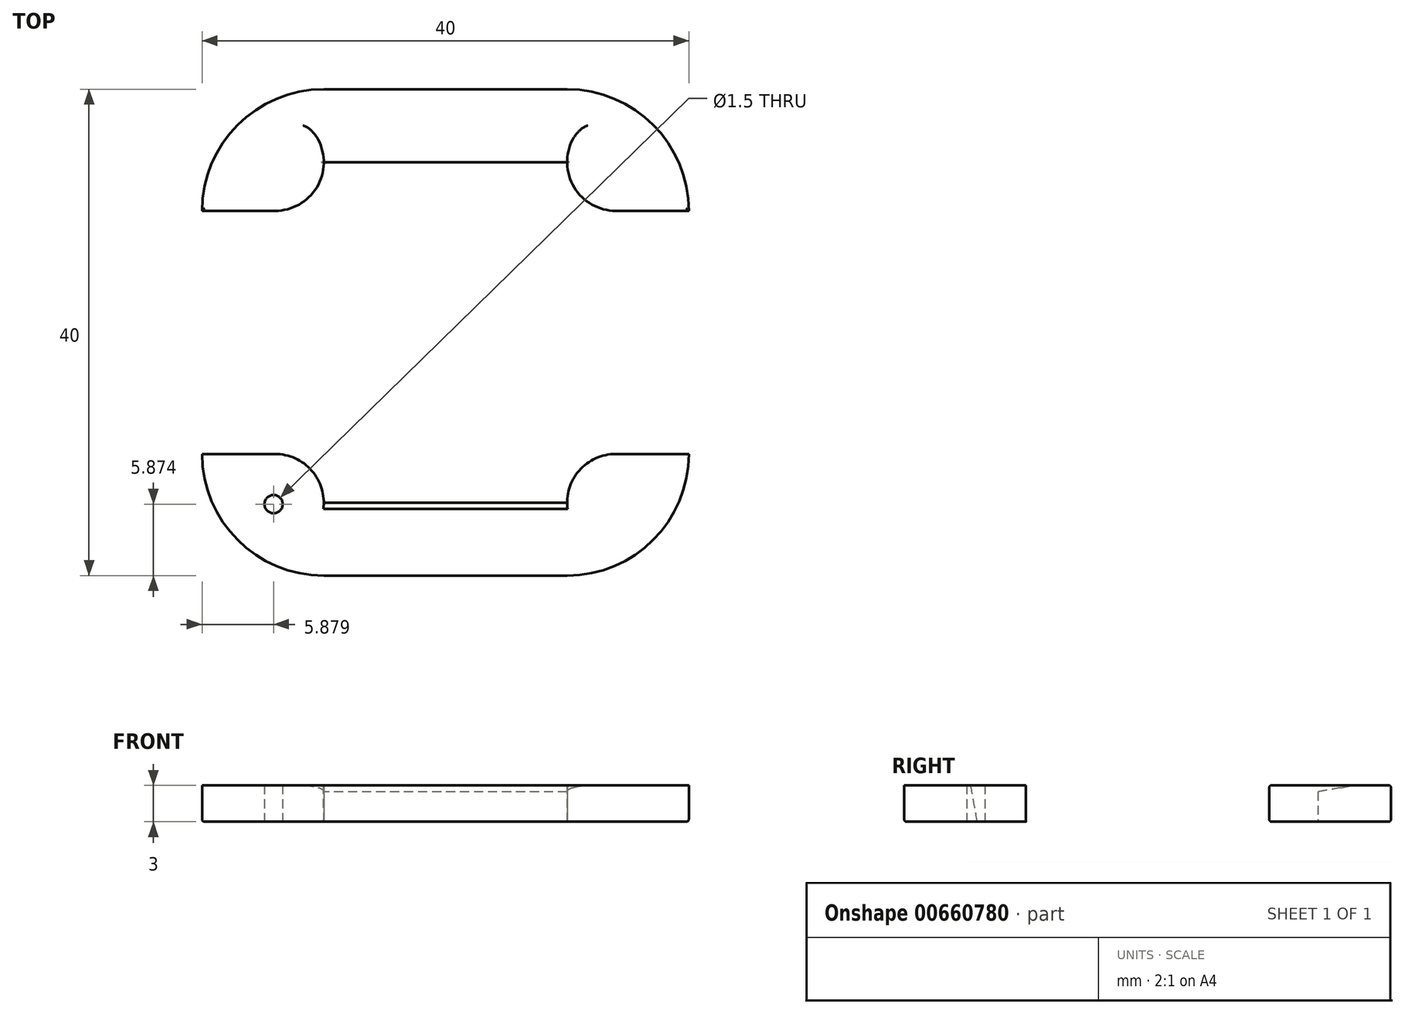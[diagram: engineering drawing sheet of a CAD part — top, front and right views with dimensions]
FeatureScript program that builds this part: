
annotation { "Feature Type Name" : "Feature", "Feature Type Description" : "" }
export const myFeature = defineFeature(function(context is Context, id is Id, definition is map)
    precondition{}
    {
        {
            var Q0;
            Q0=qCreatedBy(makeId("Top.planeOp"),FACE);
            var sketch = newSketch(context, id + "F0", { "sketchPlane" : qUnion([Q0])});
            skLineSegment(sketch, "E0.bottom", {"start": v(-41.1, 15.45) * mm, "end": v(-31.1, 15.45) * mm});
            skLineSegment(sketch, "E0.top", {"start": v(-41.1, 5.45) * mm, "end": v(-31.1, 5.45) * mm});
            skLineSegment(sketch, "E0.left", {"start": v(-41.1, 15.45) * mm, "end": v(-41.1, 5.45) * mm});
            skLineSegment(sketch, "E0.right", {"start": v(-31.1, 15.45) * mm, "end": v(-31.1, 5.45) * mm});
            skLineSegment(sketch, "E1.bottom", {"start": v(-31.1, 15.45) * mm, "end": v(-11.1, 15.45) * mm});
            skLineSegment(sketch, "E1.top", {"start": v(-31.1, 9.45) * mm, "end": v(-11.1, 9.45) * mm});
            skLineSegment(sketch, "E1.left", {"start": v(-31.1, 15.45) * mm, "end": v(-31.1, 9.45) * mm});
            skLineSegment(sketch, "E1.right", {"start": v(-11.1, 15.45) * mm, "end": v(-11.1, 9.45) * mm});
            skLineSegment(sketch, "E2.bottom", {"start": v(-11.1, 15.45) * mm, "end": v(-1.1, 15.45) * mm});
            skLineSegment(sketch, "E2.top", {"start": v(-11.1, 5.45) * mm, "end": v(-1.1, 5.45) * mm});
            skLineSegment(sketch, "E2.left", {"start": v(-11.1, 15.45) * mm, "end": v(-11.1, 5.45) * mm});
            skLineSegment(sketch, "E2.right", {"start": v(-1.1, 15.45) * mm, "end": v(-1.1, 5.45) * mm});
            skLineSegment(sketch, "E3.bottom", {"start": v(-7.1, 5.45) * mm, "end": v(-1.1, 5.45) * mm});
            skLineSegment(sketch, "E3.top", {"start": v(-7.1, -14.55) * mm, "end": v(-1.1, -14.55) * mm});
            skLineSegment(sketch, "E3.left", {"start": v(-7.1, 5.45) * mm, "end": v(-7.1, -14.55) * mm});
            skLineSegment(sketch, "E3.right", {"start": v(-1.1, 5.45) * mm, "end": v(-1.1, -14.55) * mm});
            skLineSegment(sketch, "E4.bottom", {"start": v(-11.1, -14.55) * mm, "end": v(-1.1, -14.55) * mm});
            skLineSegment(sketch, "E4.top", {"start": v(-11.1, -24.55) * mm, "end": v(-1.1, -24.55) * mm});
            skLineSegment(sketch, "E4.left", {"start": v(-11.1, -14.55) * mm, "end": v(-11.1, -24.55) * mm});
            skLineSegment(sketch, "E4.right", {"start": v(-1.1, -14.55) * mm, "end": v(-1.1, -24.55) * mm});
            skLineSegment(sketch, "E5.bottom", {"start": v(-31.1, -18.55) * mm, "end": v(-11.1, -18.55) * mm});
            skLineSegment(sketch, "E5.top", {"start": v(-31.1, -24.55) * mm, "end": v(-11.1, -24.55) * mm});
            skLineSegment(sketch, "E5.left", {"start": v(-31.1, -18.55) * mm, "end": v(-31.1, -24.55) * mm});
            skLineSegment(sketch, "E5.right", {"start": v(-11.1, -18.55) * mm, "end": v(-11.1, -24.55) * mm});
            skLineSegment(sketch, "E6.bottom", {"start": v(-41.1, -14.55) * mm, "end": v(-31.1, -14.55) * mm});
            skLineSegment(sketch, "E6.top", {"start": v(-41.1, -24.55) * mm, "end": v(-31.1, -24.55) * mm});
            skLineSegment(sketch, "E6.left", {"start": v(-41.1, -14.55) * mm, "end": v(-41.1, -24.55) * mm});
            skLineSegment(sketch, "E6.right", {"start": v(-31.1, -14.55) * mm, "end": v(-31.1, -24.55) * mm});
            skLineSegment(sketch, "E7.bottom", {"start": v(-41.1, 5.45) * mm, "end": v(-35.1, 5.45) * mm});
            skLineSegment(sketch, "E7.top", {"start": v(-41.1, -14.55) * mm, "end": v(-35.1, -14.55) * mm});
            skLineSegment(sketch, "E7.left", {"start": v(-41.1, 5.45) * mm, "end": v(-41.1, -14.55) * mm});
            skLineSegment(sketch, "E7.right", {"start": v(-35.1, 5.45) * mm, "end": v(-35.1, -14.55) * mm});
            skCircle(sketch, "E8", {"center": v(-35.22, -18.68) * mm, "radius": 0.75 * mm});
            skSolve(sketch);
        }
        {
            var Q0;
            Q0=makeQuery(id+"F0.imprint","IMPRINT",FACE,{"disambiguationData":[TD([[makeQuery(id+"F0.imprint","IMPRINT",EDGE,{"derivedFrom":sQuery(id+"F0.wireOp",EDGE,"E0.bottom")}),-1.0]])]});
            var Q1;
            {var subQ0=sQuery(id+"F0.wireOp",EDGE,"E1.bottom");Q1=makeQuery(id+"F0.imprint","IMPRINT",FACE,{"disambiguationData":[TD([[makeQuery(id+"F0.imprint","IMPRINT",EDGE,{"derivedFrom":subQ0}),-1.0]])]});}
            var Q2;
            {var subQ3=sQuery(id+"F0.wireOp",EDGE,"E2.bottom");Q2=makeQuery(id+"F0.imprint","IMPRINT",FACE,{"disambiguationData":[TD([[makeQuery(id+"F0.imprint","IMPRINT",EDGE,{"derivedFrom":subQ3}),-1.0]])]});}
            var Q3;
            Q3=makeQuery(id+"F0.imprint","IMPRINT",FACE,{"disambiguationData":[TD([[makeQuery(id+"F0.imprint","IMPRINT",EDGE,{"derivedFrom":sQuery(id+"F0.wireOp",EDGE,"E3.bottom")}),-1.0]])]});
            var Q4;
            Q4=makeQuery(id+"F0.imprint","IMPRINT",FACE,{"disambiguationData":[TD([[makeQuery(id+"F0.imprint","IMPRINT",EDGE,{"derivedFrom":sQuery(id+"F0.wireOp",EDGE,"E4.top")}),1.0]])]});
            var Q5;
            {var subQ0=sQuery(id+"F0.wireOp",EDGE,"E5.bottom");Q5=makeQuery(id+"F0.imprint","IMPRINT",FACE,{"disambiguationData":[TD([[makeQuery(id+"F0.imprint","IMPRINT",EDGE,{"derivedFrom":subQ0}),-1.0]])]});}
            var Q6;
            {var subQ2=sQuery(id+"F0.wireOp",EDGE,"E6.bottom");Q6=makeQuery(id+"F0.imprint","IMPRINT",FACE,{"disambiguationData":[TD([[makeQuery(id+"F0.imprint","IMPRINT",EDGE,{"derivedFrom":subQ2}),-1.0]])]});}
            var Q7;
            Q7=makeQuery(id+"F0.imprint","IMPRINT",FACE,{"disambiguationData":[TD([[makeQuery(id+"F0.imprint","IMPRINT",EDGE,{"derivedFrom":sQuery(id+"F0.wireOp",EDGE,"E7.bottom")}),-1.0]])]});
            extrude(context, id + "F1", {"entities" : qUnion([Q0, Q1, Q2, Q3, Q4, Q5, Q6, Q7]), "depth" : 3 * mm, "offsetDistance" : 25 * mm});
        }
        {
            var Q0;
            Q0=makeQuery(id+"F1.opExtrude","SWEPT_EDGE",EDGE,{"disambiguationData":[OSD([sQuery(id+"F0.wireOp",EDGE,"E6.top"),sQuery(id+"F0.wireOp",EDGE,"E6.left")])]});
            var Q1;
            Q1=makeQuery(id+"F1.opExtrude","SWEPT_EDGE",EDGE,{"disambiguationData":[OSD([sQuery(id+"F0.wireOp",EDGE,"E4.top"),sQuery(id+"F0.wireOp",EDGE,"E4.right")])]});
            var Q2;
            Q2=makeQuery(id+"F1.opExtrude","SWEPT_EDGE",EDGE,{"disambiguationData":[OSD([sQuery(id+"F0.wireOp",EDGE,"E2.bottom"),sQuery(id+"F0.wireOp",EDGE,"E2.right")])]});
            var Q3;
            Q3=makeQuery(id+"F1.opExtrude","SWEPT_EDGE",EDGE,{"disambiguationData":[OSD([sQuery(id+"F0.wireOp",EDGE,"E0.bottom"),sQuery(id+"F0.wireOp",EDGE,"E0.left")])]});
            fillet(context, id + "F2", {"entities" : qUnion([Q0, Q1, Q2, Q3]), "radius" : 10 * mm, "tangentPropagation" : true, "allowEdgeOverflow" : false});
        }
        {
            var Q0;
            Q0=makeQuery(id+"F1.opExtrude","SWEPT_EDGE",EDGE,{"disambiguationData":[OSD([sQuery(id+"F0.wireOp",EDGE,"E0.top"),sQuery(id+"F0.wireOp",EDGE,"E0.right")])]});
            var Q1;
            Q1=makeQuery(id+"F1.opExtrude","SWEPT_EDGE",EDGE,{"disambiguationData":[OSD([sQuery(id+"F0.wireOp",EDGE,"E2.top"),sQuery(id+"F0.wireOp",EDGE,"E2.left")])]});
            var Q2;
            Q2=makeQuery(id+"F1.opExtrude","SWEPT_EDGE",EDGE,{"disambiguationData":[OSD([sQuery(id+"F0.wireOp",EDGE,"E4.bottom"),sQuery(id+"F0.wireOp",EDGE,"E4.left")])]});
            var Q3;
            Q3=makeQuery(id+"F1.opExtrude","SWEPT_EDGE",EDGE,{"disambiguationData":[OSD([sQuery(id+"F0.wireOp",EDGE,"E6.bottom"),sQuery(id+"F0.wireOp",EDGE,"E6.right")])]});
            fillet(context, id + "F3", {"entities" : qUnion([Q0, Q1, Q2, Q3]), "radius" : 4 * mm, "tangentPropagation" : true, "allowEdgeOverflow" : false});
        }
        {
            var Q0;
            Q0=makeQuery(id+"F1.opExtrude","CAP_EDGE",EDGE,{"disambiguationData":[OSD([sQuery(id+"F0.wireOp",EDGE,"E7.right")])],"isStart":false});
            var Q1;
            Q1=makeQuery(id+"F1.opExtrude","CAP_EDGE",EDGE,{"disambiguationData":[OSD([sQuery(id+"F0.wireOp",EDGE,"E1.top")])],"isStart":false});
            var Q2;
            Q2=makeQuery(id+"F1.opExtrude","CAP_EDGE",EDGE,{"disambiguationData":[OSD([sQuery(id+"F0.wireOp",EDGE,"E3.left")])],"isStart":false});
            var Q3;
            Q3=makeQuery(id+"F1.opExtrude","CAP_EDGE",EDGE,{"disambiguationData":[OSD([sQuery(id+"F0.wireOp",EDGE,"E5.bottom")])],"isStart":false});
            chamfer(context, id + "F4", {"entities" : qUnion([Q0, Q1, Q2, Q3]), "chamferType" : ChamferType.OFFSET_ANGLE, "width" : 3 * mm, "oppositeDirection" : false, "angle" : 10 * degree, "tangentPropagation" : true});
        }
        {
            var Q0;
            Q0=makeQuery(id+"F1.opExtrude","CAP_EDGE",EDGE,{"disambiguationData":[OSD([sQuery(id+"F0.wireOp",EDGE,"E4.top"),sQuery(id+"F0.wireOp",EDGE,"E5.top"),sQuery(id+"F0.wireOp",EDGE,"E6.top")])],"isStart":true});
            var Q1;
            Q1=makeQuery(id+"F1.opExtrude","CAP_FACE",FACE,{"disambiguationData":[OSD([sQuery(id+"F0.wireOp",EDGE,"E0.bottom"),sQuery(id+"F0.wireOp",EDGE,"E0.top"),sQuery(id+"F0.wireOp",EDGE,"E0.left"),sQuery(id+"F0.wireOp",EDGE,"E0.right"),sQuery(id+"F0.wireOp",EDGE,"E1.bottom"),sQuery(id+"F0.wireOp",EDGE,"E1.top"),sQuery(id+"F0.wireOp",EDGE,"E2.bottom"),sQuery(id+"F0.wireOp",EDGE,"E2.top"),sQuery(id+"F0.wireOp",EDGE,"E2.left"),sQuery(id+"F0.wireOp",EDGE,"E2.right"),sQuery(id+"F0.wireOp",EDGE,"E3.left"),sQuery(id+"F0.wireOp",EDGE,"E3.right"),sQuery(id+"F0.wireOp",EDGE,"E4.bottom"),sQuery(id+"F0.wireOp",EDGE,"E4.top"),sQuery(id+"F0.wireOp",EDGE,"E4.left"),sQuery(id+"F0.wireOp",EDGE,"E4.right"),sQuery(id+"F0.wireOp",EDGE,"E5.bottom"),sQuery(id+"F0.wireOp",EDGE,"E5.top"),sQuery(id+"F0.wireOp",EDGE,"E6.bottom"),sQuery(id+"F0.wireOp",EDGE,"E6.top"),sQuery(id+"F0.wireOp",EDGE,"E6.left"),sQuery(id+"F0.wireOp",EDGE,"E6.right"),sQuery(id+"F0.wireOp",EDGE,"E7.left"),sQuery(id+"F0.wireOp",EDGE,"E7.right"),sQuery(id+"F0.wireOp",EDGE,"E8")])],"isStart":false});
            var Q2;
            {var subQ0=sQuery(id+"F0.wireOp",EDGE,"E6.right");var subQ1=sQuery(id+"F0.wireOp",EDGE,"E6.bottom");Q2=makeQuery(id+"F3.opFillet","BLEND_EDGE",EDGE,{"blendedFrom":[makeQuery(id+"F1.opExtrude","SWEPT_EDGE",EDGE,{"disambiguationData":[OSD([subQ1,subQ0])]}),makeQuery(id+"F1.opExtrude","CAP_FACE",FACE,{"disambiguationData":[OSD([sQuery(id+"F0.wireOp",EDGE,"E0.bottom"),sQuery(id+"F0.wireOp",EDGE,"E0.top"),sQuery(id+"F0.wireOp",EDGE,"E0.left"),sQuery(id+"F0.wireOp",EDGE,"E0.right"),sQuery(id+"F0.wireOp",EDGE,"E1.bottom"),sQuery(id+"F0.wireOp",EDGE,"E1.top"),sQuery(id+"F0.wireOp",EDGE,"E2.bottom"),sQuery(id+"F0.wireOp",EDGE,"E2.top"),sQuery(id+"F0.wireOp",EDGE,"E2.left"),sQuery(id+"F0.wireOp",EDGE,"E2.right"),sQuery(id+"F0.wireOp",EDGE,"E3.left"),sQuery(id+"F0.wireOp",EDGE,"E3.right"),sQuery(id+"F0.wireOp",EDGE,"E4.bottom"),sQuery(id+"F0.wireOp",EDGE,"E4.top"),sQuery(id+"F0.wireOp",EDGE,"E4.left"),sQuery(id+"F0.wireOp",EDGE,"E4.right"),sQuery(id+"F0.wireOp",EDGE,"E5.bottom"),sQuery(id+"F0.wireOp",EDGE,"E5.top"),subQ1,sQuery(id+"F0.wireOp",EDGE,"E6.top"),sQuery(id+"F0.wireOp",EDGE,"E6.left"),subQ0,sQuery(id+"F0.wireOp",EDGE,"E7.left"),sQuery(id+"F0.wireOp",EDGE,"E7.right"),sQuery(id+"F0.wireOp",EDGE,"E8")])],"isStart":true})],"blendedInto":[makeQuery(id+"F1.opExtrude","CAP_FACE",FACE,{"disambiguationData":[OSD([sQuery(id+"F0.wireOp",EDGE,"E0.bottom"),sQuery(id+"F0.wireOp",EDGE,"E0.top"),sQuery(id+"F0.wireOp",EDGE,"E0.left"),sQuery(id+"F0.wireOp",EDGE,"E0.right"),sQuery(id+"F0.wireOp",EDGE,"E1.bottom"),sQuery(id+"F0.wireOp",EDGE,"E1.top"),sQuery(id+"F0.wireOp",EDGE,"E2.bottom"),sQuery(id+"F0.wireOp",EDGE,"E2.top"),sQuery(id+"F0.wireOp",EDGE,"E2.left"),sQuery(id+"F0.wireOp",EDGE,"E2.right"),sQuery(id+"F0.wireOp",EDGE,"E3.left"),sQuery(id+"F0.wireOp",EDGE,"E3.right"),sQuery(id+"F0.wireOp",EDGE,"E4.bottom"),sQuery(id+"F0.wireOp",EDGE,"E4.top"),sQuery(id+"F0.wireOp",EDGE,"E4.left"),sQuery(id+"F0.wireOp",EDGE,"E4.right"),sQuery(id+"F0.wireOp",EDGE,"E5.bottom"),sQuery(id+"F0.wireOp",EDGE,"E5.top"),subQ1,sQuery(id+"F0.wireOp",EDGE,"E6.top"),sQuery(id+"F0.wireOp",EDGE,"E6.left"),subQ0,sQuery(id+"F0.wireOp",EDGE,"E7.left"),sQuery(id+"F0.wireOp",EDGE,"E7.right"),sQuery(id+"F0.wireOp",EDGE,"E8")])],"isStart":true})]});}
            var Q3;
            {var subQ0=sQuery(id+"F0.wireOp",EDGE,"E4.left");var subQ1=sQuery(id+"F0.wireOp",EDGE,"E4.bottom");Q3=makeQuery(id+"F3.opFillet","BLEND_EDGE",EDGE,{"blendedFrom":[makeQuery(id+"F1.opExtrude","SWEPT_EDGE",EDGE,{"disambiguationData":[OSD([subQ1,subQ0])]}),makeQuery(id+"F1.opExtrude","CAP_FACE",FACE,{"disambiguationData":[OSD([sQuery(id+"F0.wireOp",EDGE,"E0.bottom"),sQuery(id+"F0.wireOp",EDGE,"E0.top"),sQuery(id+"F0.wireOp",EDGE,"E0.left"),sQuery(id+"F0.wireOp",EDGE,"E0.right"),sQuery(id+"F0.wireOp",EDGE,"E1.bottom"),sQuery(id+"F0.wireOp",EDGE,"E1.top"),sQuery(id+"F0.wireOp",EDGE,"E2.bottom"),sQuery(id+"F0.wireOp",EDGE,"E2.top"),sQuery(id+"F0.wireOp",EDGE,"E2.left"),sQuery(id+"F0.wireOp",EDGE,"E2.right"),sQuery(id+"F0.wireOp",EDGE,"E3.left"),sQuery(id+"F0.wireOp",EDGE,"E3.right"),subQ1,sQuery(id+"F0.wireOp",EDGE,"E4.top"),subQ0,sQuery(id+"F0.wireOp",EDGE,"E4.right"),sQuery(id+"F0.wireOp",EDGE,"E5.bottom"),sQuery(id+"F0.wireOp",EDGE,"E5.top"),sQuery(id+"F0.wireOp",EDGE,"E6.bottom"),sQuery(id+"F0.wireOp",EDGE,"E6.top"),sQuery(id+"F0.wireOp",EDGE,"E6.left"),sQuery(id+"F0.wireOp",EDGE,"E6.right"),sQuery(id+"F0.wireOp",EDGE,"E7.left"),sQuery(id+"F0.wireOp",EDGE,"E7.right"),sQuery(id+"F0.wireOp",EDGE,"E8")])],"isStart":true})],"blendedInto":[makeQuery(id+"F1.opExtrude","CAP_FACE",FACE,{"disambiguationData":[OSD([sQuery(id+"F0.wireOp",EDGE,"E0.bottom"),sQuery(id+"F0.wireOp",EDGE,"E0.top"),sQuery(id+"F0.wireOp",EDGE,"E0.left"),sQuery(id+"F0.wireOp",EDGE,"E0.right"),sQuery(id+"F0.wireOp",EDGE,"E1.bottom"),sQuery(id+"F0.wireOp",EDGE,"E1.top"),sQuery(id+"F0.wireOp",EDGE,"E2.bottom"),sQuery(id+"F0.wireOp",EDGE,"E2.top"),sQuery(id+"F0.wireOp",EDGE,"E2.left"),sQuery(id+"F0.wireOp",EDGE,"E2.right"),sQuery(id+"F0.wireOp",EDGE,"E3.left"),sQuery(id+"F0.wireOp",EDGE,"E3.right"),subQ1,sQuery(id+"F0.wireOp",EDGE,"E4.top"),subQ0,sQuery(id+"F0.wireOp",EDGE,"E4.right"),sQuery(id+"F0.wireOp",EDGE,"E5.bottom"),sQuery(id+"F0.wireOp",EDGE,"E5.top"),sQuery(id+"F0.wireOp",EDGE,"E6.bottom"),sQuery(id+"F0.wireOp",EDGE,"E6.top"),sQuery(id+"F0.wireOp",EDGE,"E6.left"),sQuery(id+"F0.wireOp",EDGE,"E6.right"),sQuery(id+"F0.wireOp",EDGE,"E7.left"),sQuery(id+"F0.wireOp",EDGE,"E7.right"),sQuery(id+"F0.wireOp",EDGE,"E8")])],"isStart":true})]});}
            var Q4;
            {var subQ0=sQuery(id+"F0.wireOp",EDGE,"E2.left");var subQ1=sQuery(id+"F0.wireOp",EDGE,"E2.top");Q4=makeQuery(id+"F3.opFillet","BLEND_EDGE",EDGE,{"blendedFrom":[makeQuery(id+"F1.opExtrude","SWEPT_EDGE",EDGE,{"disambiguationData":[OSD([subQ1,subQ0])]}),makeQuery(id+"F1.opExtrude","CAP_FACE",FACE,{"disambiguationData":[OSD([sQuery(id+"F0.wireOp",EDGE,"E0.bottom"),sQuery(id+"F0.wireOp",EDGE,"E0.top"),sQuery(id+"F0.wireOp",EDGE,"E0.left"),sQuery(id+"F0.wireOp",EDGE,"E0.right"),sQuery(id+"F0.wireOp",EDGE,"E1.bottom"),sQuery(id+"F0.wireOp",EDGE,"E1.top"),sQuery(id+"F0.wireOp",EDGE,"E2.bottom"),subQ1,subQ0,sQuery(id+"F0.wireOp",EDGE,"E2.right"),sQuery(id+"F0.wireOp",EDGE,"E3.left"),sQuery(id+"F0.wireOp",EDGE,"E3.right"),sQuery(id+"F0.wireOp",EDGE,"E4.bottom"),sQuery(id+"F0.wireOp",EDGE,"E4.top"),sQuery(id+"F0.wireOp",EDGE,"E4.left"),sQuery(id+"F0.wireOp",EDGE,"E4.right"),sQuery(id+"F0.wireOp",EDGE,"E5.bottom"),sQuery(id+"F0.wireOp",EDGE,"E5.top"),sQuery(id+"F0.wireOp",EDGE,"E6.bottom"),sQuery(id+"F0.wireOp",EDGE,"E6.top"),sQuery(id+"F0.wireOp",EDGE,"E6.left"),sQuery(id+"F0.wireOp",EDGE,"E6.right"),sQuery(id+"F0.wireOp",EDGE,"E7.left"),sQuery(id+"F0.wireOp",EDGE,"E7.right"),sQuery(id+"F0.wireOp",EDGE,"E8")])],"isStart":true})],"blendedInto":[makeQuery(id+"F1.opExtrude","CAP_FACE",FACE,{"disambiguationData":[OSD([sQuery(id+"F0.wireOp",EDGE,"E0.bottom"),sQuery(id+"F0.wireOp",EDGE,"E0.top"),sQuery(id+"F0.wireOp",EDGE,"E0.left"),sQuery(id+"F0.wireOp",EDGE,"E0.right"),sQuery(id+"F0.wireOp",EDGE,"E1.bottom"),sQuery(id+"F0.wireOp",EDGE,"E1.top"),sQuery(id+"F0.wireOp",EDGE,"E2.bottom"),subQ1,subQ0,sQuery(id+"F0.wireOp",EDGE,"E2.right"),sQuery(id+"F0.wireOp",EDGE,"E3.left"),sQuery(id+"F0.wireOp",EDGE,"E3.right"),sQuery(id+"F0.wireOp",EDGE,"E4.bottom"),sQuery(id+"F0.wireOp",EDGE,"E4.top"),sQuery(id+"F0.wireOp",EDGE,"E4.left"),sQuery(id+"F0.wireOp",EDGE,"E4.right"),sQuery(id+"F0.wireOp",EDGE,"E5.bottom"),sQuery(id+"F0.wireOp",EDGE,"E5.top"),sQuery(id+"F0.wireOp",EDGE,"E6.bottom"),sQuery(id+"F0.wireOp",EDGE,"E6.top"),sQuery(id+"F0.wireOp",EDGE,"E6.left"),sQuery(id+"F0.wireOp",EDGE,"E6.right"),sQuery(id+"F0.wireOp",EDGE,"E7.left"),sQuery(id+"F0.wireOp",EDGE,"E7.right"),sQuery(id+"F0.wireOp",EDGE,"E8")])],"isStart":true})]});}
            var Q5;
            {var subQ0=sQuery(id+"F0.wireOp",EDGE,"E0.right");var subQ1=sQuery(id+"F0.wireOp",EDGE,"E0.top");Q5=makeQuery(id+"F3.opFillet","BLEND_EDGE",EDGE,{"blendedFrom":[makeQuery(id+"F1.opExtrude","SWEPT_EDGE",EDGE,{"disambiguationData":[OSD([subQ1,subQ0])]}),makeQuery(id+"F1.opExtrude","CAP_FACE",FACE,{"disambiguationData":[OSD([sQuery(id+"F0.wireOp",EDGE,"E0.bottom"),subQ1,sQuery(id+"F0.wireOp",EDGE,"E0.left"),subQ0,sQuery(id+"F0.wireOp",EDGE,"E1.bottom"),sQuery(id+"F0.wireOp",EDGE,"E1.top"),sQuery(id+"F0.wireOp",EDGE,"E2.bottom"),sQuery(id+"F0.wireOp",EDGE,"E2.top"),sQuery(id+"F0.wireOp",EDGE,"E2.left"),sQuery(id+"F0.wireOp",EDGE,"E2.right"),sQuery(id+"F0.wireOp",EDGE,"E3.left"),sQuery(id+"F0.wireOp",EDGE,"E3.right"),sQuery(id+"F0.wireOp",EDGE,"E4.bottom"),sQuery(id+"F0.wireOp",EDGE,"E4.top"),sQuery(id+"F0.wireOp",EDGE,"E4.left"),sQuery(id+"F0.wireOp",EDGE,"E4.right"),sQuery(id+"F0.wireOp",EDGE,"E5.bottom"),sQuery(id+"F0.wireOp",EDGE,"E5.top"),sQuery(id+"F0.wireOp",EDGE,"E6.bottom"),sQuery(id+"F0.wireOp",EDGE,"E6.top"),sQuery(id+"F0.wireOp",EDGE,"E6.left"),sQuery(id+"F0.wireOp",EDGE,"E6.right"),sQuery(id+"F0.wireOp",EDGE,"E7.left"),sQuery(id+"F0.wireOp",EDGE,"E7.right"),sQuery(id+"F0.wireOp",EDGE,"E8")])],"isStart":true})],"blendedInto":[makeQuery(id+"F1.opExtrude","CAP_FACE",FACE,{"disambiguationData":[OSD([sQuery(id+"F0.wireOp",EDGE,"E0.bottom"),subQ1,sQuery(id+"F0.wireOp",EDGE,"E0.left"),subQ0,sQuery(id+"F0.wireOp",EDGE,"E1.bottom"),sQuery(id+"F0.wireOp",EDGE,"E1.top"),sQuery(id+"F0.wireOp",EDGE,"E2.bottom"),sQuery(id+"F0.wireOp",EDGE,"E2.top"),sQuery(id+"F0.wireOp",EDGE,"E2.left"),sQuery(id+"F0.wireOp",EDGE,"E2.right"),sQuery(id+"F0.wireOp",EDGE,"E3.left"),sQuery(id+"F0.wireOp",EDGE,"E3.right"),sQuery(id+"F0.wireOp",EDGE,"E4.bottom"),sQuery(id+"F0.wireOp",EDGE,"E4.top"),sQuery(id+"F0.wireOp",EDGE,"E4.left"),sQuery(id+"F0.wireOp",EDGE,"E4.right"),sQuery(id+"F0.wireOp",EDGE,"E5.bottom"),sQuery(id+"F0.wireOp",EDGE,"E5.top"),sQuery(id+"F0.wireOp",EDGE,"E6.bottom"),sQuery(id+"F0.wireOp",EDGE,"E6.top"),sQuery(id+"F0.wireOp",EDGE,"E6.left"),sQuery(id+"F0.wireOp",EDGE,"E6.right"),sQuery(id+"F0.wireOp",EDGE,"E7.left"),sQuery(id+"F0.wireOp",EDGE,"E7.right"),sQuery(id+"F0.wireOp",EDGE,"E8")])],"isStart":true})]});}
            var Q6;
            Q6=makeQuery(id+"F1.opExtrude","CAP_EDGE",EDGE,{"disambiguationData":[OSD([sQuery(id+"F0.wireOp",EDGE,"E2.right"),sQuery(id+"F0.wireOp",EDGE,"E3.right"),sQuery(id+"F0.wireOp",EDGE,"E4.right")])],"isStart":true});
            var Q7;
            {var subQ0=sQuery(id+"F0.wireOp",EDGE,"E2.right");var subQ1=sQuery(id+"F0.wireOp",EDGE,"E2.bottom");Q7=makeQuery(id+"F2.opFillet","BLEND_EDGE",EDGE,{"blendedFrom":[makeQuery(id+"F1.opExtrude","SWEPT_EDGE",EDGE,{"disambiguationData":[OSD([subQ1,subQ0])]}),makeQuery(id+"F1.opExtrude","CAP_FACE",FACE,{"disambiguationData":[OSD([sQuery(id+"F0.wireOp",EDGE,"E0.bottom"),sQuery(id+"F0.wireOp",EDGE,"E0.top"),sQuery(id+"F0.wireOp",EDGE,"E0.left"),sQuery(id+"F0.wireOp",EDGE,"E0.right"),sQuery(id+"F0.wireOp",EDGE,"E1.bottom"),sQuery(id+"F0.wireOp",EDGE,"E1.top"),subQ1,sQuery(id+"F0.wireOp",EDGE,"E2.top"),sQuery(id+"F0.wireOp",EDGE,"E2.left"),subQ0,sQuery(id+"F0.wireOp",EDGE,"E3.left"),sQuery(id+"F0.wireOp",EDGE,"E3.right"),sQuery(id+"F0.wireOp",EDGE,"E4.bottom"),sQuery(id+"F0.wireOp",EDGE,"E4.top"),sQuery(id+"F0.wireOp",EDGE,"E4.left"),sQuery(id+"F0.wireOp",EDGE,"E4.right"),sQuery(id+"F0.wireOp",EDGE,"E5.bottom"),sQuery(id+"F0.wireOp",EDGE,"E5.top"),sQuery(id+"F0.wireOp",EDGE,"E6.bottom"),sQuery(id+"F0.wireOp",EDGE,"E6.top"),sQuery(id+"F0.wireOp",EDGE,"E6.left"),sQuery(id+"F0.wireOp",EDGE,"E6.right"),sQuery(id+"F0.wireOp",EDGE,"E7.left"),sQuery(id+"F0.wireOp",EDGE,"E7.right"),sQuery(id+"F0.wireOp",EDGE,"E8")])],"isStart":true})],"blendedInto":[makeQuery(id+"F1.opExtrude","CAP_FACE",FACE,{"disambiguationData":[OSD([sQuery(id+"F0.wireOp",EDGE,"E0.bottom"),sQuery(id+"F0.wireOp",EDGE,"E0.top"),sQuery(id+"F0.wireOp",EDGE,"E0.left"),sQuery(id+"F0.wireOp",EDGE,"E0.right"),sQuery(id+"F0.wireOp",EDGE,"E1.bottom"),sQuery(id+"F0.wireOp",EDGE,"E1.top"),subQ1,sQuery(id+"F0.wireOp",EDGE,"E2.top"),sQuery(id+"F0.wireOp",EDGE,"E2.left"),subQ0,sQuery(id+"F0.wireOp",EDGE,"E3.left"),sQuery(id+"F0.wireOp",EDGE,"E3.right"),sQuery(id+"F0.wireOp",EDGE,"E4.bottom"),sQuery(id+"F0.wireOp",EDGE,"E4.top"),sQuery(id+"F0.wireOp",EDGE,"E4.left"),sQuery(id+"F0.wireOp",EDGE,"E4.right"),sQuery(id+"F0.wireOp",EDGE,"E5.bottom"),sQuery(id+"F0.wireOp",EDGE,"E5.top"),sQuery(id+"F0.wireOp",EDGE,"E6.bottom"),sQuery(id+"F0.wireOp",EDGE,"E6.top"),sQuery(id+"F0.wireOp",EDGE,"E6.left"),sQuery(id+"F0.wireOp",EDGE,"E6.right"),sQuery(id+"F0.wireOp",EDGE,"E7.left"),sQuery(id+"F0.wireOp",EDGE,"E7.right"),sQuery(id+"F0.wireOp",EDGE,"E8")])],"isStart":true})]});}
            var Q8;
            {var subQ0=sQuery(id+"F0.wireOp",EDGE,"E4.right");var subQ1=sQuery(id+"F0.wireOp",EDGE,"E4.top");Q8=makeQuery(id+"F2.opFillet","BLEND_EDGE",EDGE,{"blendedFrom":[makeQuery(id+"F1.opExtrude","SWEPT_EDGE",EDGE,{"disambiguationData":[OSD([subQ1,subQ0])]}),makeQuery(id+"F1.opExtrude","CAP_FACE",FACE,{"disambiguationData":[OSD([sQuery(id+"F0.wireOp",EDGE,"E0.bottom"),sQuery(id+"F0.wireOp",EDGE,"E0.top"),sQuery(id+"F0.wireOp",EDGE,"E0.left"),sQuery(id+"F0.wireOp",EDGE,"E0.right"),sQuery(id+"F0.wireOp",EDGE,"E1.bottom"),sQuery(id+"F0.wireOp",EDGE,"E1.top"),sQuery(id+"F0.wireOp",EDGE,"E2.bottom"),sQuery(id+"F0.wireOp",EDGE,"E2.top"),sQuery(id+"F0.wireOp",EDGE,"E2.left"),sQuery(id+"F0.wireOp",EDGE,"E2.right"),sQuery(id+"F0.wireOp",EDGE,"E3.left"),sQuery(id+"F0.wireOp",EDGE,"E3.right"),sQuery(id+"F0.wireOp",EDGE,"E4.bottom"),subQ1,sQuery(id+"F0.wireOp",EDGE,"E4.left"),subQ0,sQuery(id+"F0.wireOp",EDGE,"E5.bottom"),sQuery(id+"F0.wireOp",EDGE,"E5.top"),sQuery(id+"F0.wireOp",EDGE,"E6.bottom"),sQuery(id+"F0.wireOp",EDGE,"E6.top"),sQuery(id+"F0.wireOp",EDGE,"E6.left"),sQuery(id+"F0.wireOp",EDGE,"E6.right"),sQuery(id+"F0.wireOp",EDGE,"E7.left"),sQuery(id+"F0.wireOp",EDGE,"E7.right"),sQuery(id+"F0.wireOp",EDGE,"E8")])],"isStart":true})],"blendedInto":[makeQuery(id+"F1.opExtrude","CAP_FACE",FACE,{"disambiguationData":[OSD([sQuery(id+"F0.wireOp",EDGE,"E0.bottom"),sQuery(id+"F0.wireOp",EDGE,"E0.top"),sQuery(id+"F0.wireOp",EDGE,"E0.left"),sQuery(id+"F0.wireOp",EDGE,"E0.right"),sQuery(id+"F0.wireOp",EDGE,"E1.bottom"),sQuery(id+"F0.wireOp",EDGE,"E1.top"),sQuery(id+"F0.wireOp",EDGE,"E2.bottom"),sQuery(id+"F0.wireOp",EDGE,"E2.top"),sQuery(id+"F0.wireOp",EDGE,"E2.left"),sQuery(id+"F0.wireOp",EDGE,"E2.right"),sQuery(id+"F0.wireOp",EDGE,"E3.left"),sQuery(id+"F0.wireOp",EDGE,"E3.right"),sQuery(id+"F0.wireOp",EDGE,"E4.bottom"),subQ1,sQuery(id+"F0.wireOp",EDGE,"E4.left"),subQ0,sQuery(id+"F0.wireOp",EDGE,"E5.bottom"),sQuery(id+"F0.wireOp",EDGE,"E5.top"),sQuery(id+"F0.wireOp",EDGE,"E6.bottom"),sQuery(id+"F0.wireOp",EDGE,"E6.top"),sQuery(id+"F0.wireOp",EDGE,"E6.left"),sQuery(id+"F0.wireOp",EDGE,"E6.right"),sQuery(id+"F0.wireOp",EDGE,"E7.left"),sQuery(id+"F0.wireOp",EDGE,"E7.right"),sQuery(id+"F0.wireOp",EDGE,"E8")])],"isStart":true})]});}
            var Q9;
            Q9=makeQuery(id+"F1.opExtrude","CAP_EDGE",EDGE,{"disambiguationData":[OSD([sQuery(id+"F0.wireOp",EDGE,"E0.bottom"),sQuery(id+"F0.wireOp",EDGE,"E1.bottom"),sQuery(id+"F0.wireOp",EDGE,"E2.bottom")])],"isStart":true});
            var Q10;
            {var subQ0=sQuery(id+"F0.wireOp",EDGE,"E0.left");var subQ1=sQuery(id+"F0.wireOp",EDGE,"E0.bottom");Q10=makeQuery(id+"F2.opFillet","BLEND_EDGE",EDGE,{"blendedFrom":[makeQuery(id+"F1.opExtrude","SWEPT_EDGE",EDGE,{"disambiguationData":[OSD([subQ1,subQ0])]}),makeQuery(id+"F1.opExtrude","CAP_FACE",FACE,{"disambiguationData":[OSD([subQ1,sQuery(id+"F0.wireOp",EDGE,"E0.top"),subQ0,sQuery(id+"F0.wireOp",EDGE,"E0.right"),sQuery(id+"F0.wireOp",EDGE,"E1.bottom"),sQuery(id+"F0.wireOp",EDGE,"E1.top"),sQuery(id+"F0.wireOp",EDGE,"E2.bottom"),sQuery(id+"F0.wireOp",EDGE,"E2.top"),sQuery(id+"F0.wireOp",EDGE,"E2.left"),sQuery(id+"F0.wireOp",EDGE,"E2.right"),sQuery(id+"F0.wireOp",EDGE,"E3.left"),sQuery(id+"F0.wireOp",EDGE,"E3.right"),sQuery(id+"F0.wireOp",EDGE,"E4.bottom"),sQuery(id+"F0.wireOp",EDGE,"E4.top"),sQuery(id+"F0.wireOp",EDGE,"E4.left"),sQuery(id+"F0.wireOp",EDGE,"E4.right"),sQuery(id+"F0.wireOp",EDGE,"E5.bottom"),sQuery(id+"F0.wireOp",EDGE,"E5.top"),sQuery(id+"F0.wireOp",EDGE,"E6.bottom"),sQuery(id+"F0.wireOp",EDGE,"E6.top"),sQuery(id+"F0.wireOp",EDGE,"E6.left"),sQuery(id+"F0.wireOp",EDGE,"E6.right"),sQuery(id+"F0.wireOp",EDGE,"E7.left"),sQuery(id+"F0.wireOp",EDGE,"E7.right"),sQuery(id+"F0.wireOp",EDGE,"E8")])],"isStart":true})],"blendedInto":[makeQuery(id+"F1.opExtrude","CAP_FACE",FACE,{"disambiguationData":[OSD([subQ1,sQuery(id+"F0.wireOp",EDGE,"E0.top"),subQ0,sQuery(id+"F0.wireOp",EDGE,"E0.right"),sQuery(id+"F0.wireOp",EDGE,"E1.bottom"),sQuery(id+"F0.wireOp",EDGE,"E1.top"),sQuery(id+"F0.wireOp",EDGE,"E2.bottom"),sQuery(id+"F0.wireOp",EDGE,"E2.top"),sQuery(id+"F0.wireOp",EDGE,"E2.left"),sQuery(id+"F0.wireOp",EDGE,"E2.right"),sQuery(id+"F0.wireOp",EDGE,"E3.left"),sQuery(id+"F0.wireOp",EDGE,"E3.right"),sQuery(id+"F0.wireOp",EDGE,"E4.bottom"),sQuery(id+"F0.wireOp",EDGE,"E4.top"),sQuery(id+"F0.wireOp",EDGE,"E4.left"),sQuery(id+"F0.wireOp",EDGE,"E4.right"),sQuery(id+"F0.wireOp",EDGE,"E5.bottom"),sQuery(id+"F0.wireOp",EDGE,"E5.top"),sQuery(id+"F0.wireOp",EDGE,"E6.bottom"),sQuery(id+"F0.wireOp",EDGE,"E6.top"),sQuery(id+"F0.wireOp",EDGE,"E6.left"),sQuery(id+"F0.wireOp",EDGE,"E6.right"),sQuery(id+"F0.wireOp",EDGE,"E7.left"),sQuery(id+"F0.wireOp",EDGE,"E7.right"),sQuery(id+"F0.wireOp",EDGE,"E8")])],"isStart":true})]});}
            var Q11;
            Q11=makeQuery(id+"F1.opExtrude","CAP_EDGE",EDGE,{"disambiguationData":[OSD([sQuery(id+"F0.wireOp",EDGE,"E0.left"),sQuery(id+"F0.wireOp",EDGE,"E6.left"),sQuery(id+"F0.wireOp",EDGE,"E7.left")])],"isStart":true});
            var Q12;
            {var subQ0=sQuery(id+"F0.wireOp",EDGE,"E6.left");var subQ1=sQuery(id+"F0.wireOp",EDGE,"E6.top");Q12=makeQuery(id+"F2.opFillet","BLEND_EDGE",EDGE,{"blendedFrom":[makeQuery(id+"F1.opExtrude","SWEPT_EDGE",EDGE,{"disambiguationData":[OSD([subQ1,subQ0])]}),makeQuery(id+"F1.opExtrude","CAP_FACE",FACE,{"disambiguationData":[OSD([sQuery(id+"F0.wireOp",EDGE,"E0.bottom"),sQuery(id+"F0.wireOp",EDGE,"E0.top"),sQuery(id+"F0.wireOp",EDGE,"E0.left"),sQuery(id+"F0.wireOp",EDGE,"E0.right"),sQuery(id+"F0.wireOp",EDGE,"E1.bottom"),sQuery(id+"F0.wireOp",EDGE,"E1.top"),sQuery(id+"F0.wireOp",EDGE,"E2.bottom"),sQuery(id+"F0.wireOp",EDGE,"E2.top"),sQuery(id+"F0.wireOp",EDGE,"E2.left"),sQuery(id+"F0.wireOp",EDGE,"E2.right"),sQuery(id+"F0.wireOp",EDGE,"E3.left"),sQuery(id+"F0.wireOp",EDGE,"E3.right"),sQuery(id+"F0.wireOp",EDGE,"E4.bottom"),sQuery(id+"F0.wireOp",EDGE,"E4.top"),sQuery(id+"F0.wireOp",EDGE,"E4.left"),sQuery(id+"F0.wireOp",EDGE,"E4.right"),sQuery(id+"F0.wireOp",EDGE,"E5.bottom"),sQuery(id+"F0.wireOp",EDGE,"E5.top"),sQuery(id+"F0.wireOp",EDGE,"E6.bottom"),subQ1,subQ0,sQuery(id+"F0.wireOp",EDGE,"E6.right"),sQuery(id+"F0.wireOp",EDGE,"E7.left"),sQuery(id+"F0.wireOp",EDGE,"E7.right"),sQuery(id+"F0.wireOp",EDGE,"E8")])],"isStart":true})],"blendedInto":[makeQuery(id+"F1.opExtrude","CAP_FACE",FACE,{"disambiguationData":[OSD([sQuery(id+"F0.wireOp",EDGE,"E0.bottom"),sQuery(id+"F0.wireOp",EDGE,"E0.top"),sQuery(id+"F0.wireOp",EDGE,"E0.left"),sQuery(id+"F0.wireOp",EDGE,"E0.right"),sQuery(id+"F0.wireOp",EDGE,"E1.bottom"),sQuery(id+"F0.wireOp",EDGE,"E1.top"),sQuery(id+"F0.wireOp",EDGE,"E2.bottom"),sQuery(id+"F0.wireOp",EDGE,"E2.top"),sQuery(id+"F0.wireOp",EDGE,"E2.left"),sQuery(id+"F0.wireOp",EDGE,"E2.right"),sQuery(id+"F0.wireOp",EDGE,"E3.left"),sQuery(id+"F0.wireOp",EDGE,"E3.right"),sQuery(id+"F0.wireOp",EDGE,"E4.bottom"),sQuery(id+"F0.wireOp",EDGE,"E4.top"),sQuery(id+"F0.wireOp",EDGE,"E4.left"),sQuery(id+"F0.wireOp",EDGE,"E4.right"),sQuery(id+"F0.wireOp",EDGE,"E5.bottom"),sQuery(id+"F0.wireOp",EDGE,"E5.top"),sQuery(id+"F0.wireOp",EDGE,"E6.bottom"),subQ1,subQ0,sQuery(id+"F0.wireOp",EDGE,"E6.right"),sQuery(id+"F0.wireOp",EDGE,"E7.left"),sQuery(id+"F0.wireOp",EDGE,"E7.right"),sQuery(id+"F0.wireOp",EDGE,"E8")])],"isStart":true})]});}
            fillet(context, id + "F5", {"entities" : qUnion([Q0, Q1, Q2, Q3, Q4, Q5, Q6, Q7, Q8, Q9, Q10, Q11, Q12]), "tangentPropagation" : true, "radius" : 0.2 * mm, "defaultsChanged" : false, "vertexSettings" : [], "allowEdgeOverflow" : false});
        }
    });
